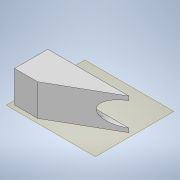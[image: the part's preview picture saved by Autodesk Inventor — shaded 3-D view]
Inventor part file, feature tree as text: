
AUTODESK INVENTOR PART (.ipt)
format: ipt  version: 2022.3 (Build 263350000, 350)  size: 117,760 bytes
history: native  units: mm
features: extrude x3, sketch x3, thicken_offset x2, other x2, plane x1, reference x1
ambient origin geometry x8: Origin, YZ Plane, XZ Plane, XY Plane, X Axis, Y Axis, Z Axis, Center Point
bodies: Solid1 (feature_tree)
feature tree (12):
  plane  "Work Plane1"
  extrude  "Extrusion1"  Depth=8.0mm
  extrude  "Extrusion2"  Depth=0.2mm
  thicken_offset  "Thicken1"
  thicken_offset  "Thicken2"
  extrude  "Extrusion3"  Depth=0.2mm
  sketch  "Sketch1"  dims[d0=8.0mm d1=0.0mm d2=6.0mm]
  reference  "Reference1"
  sketch  "Sketch2"  dims[d3=15.981mm d4=0.0mm d5=0.2mm]
  sketch  "Sketch3"  dims[d6=0.2mm d7=0.2mm d8=0.2mm d9=0.0mm d10=0.0mm]
  other  "v2.0.iam"
  other  "Base:1"
